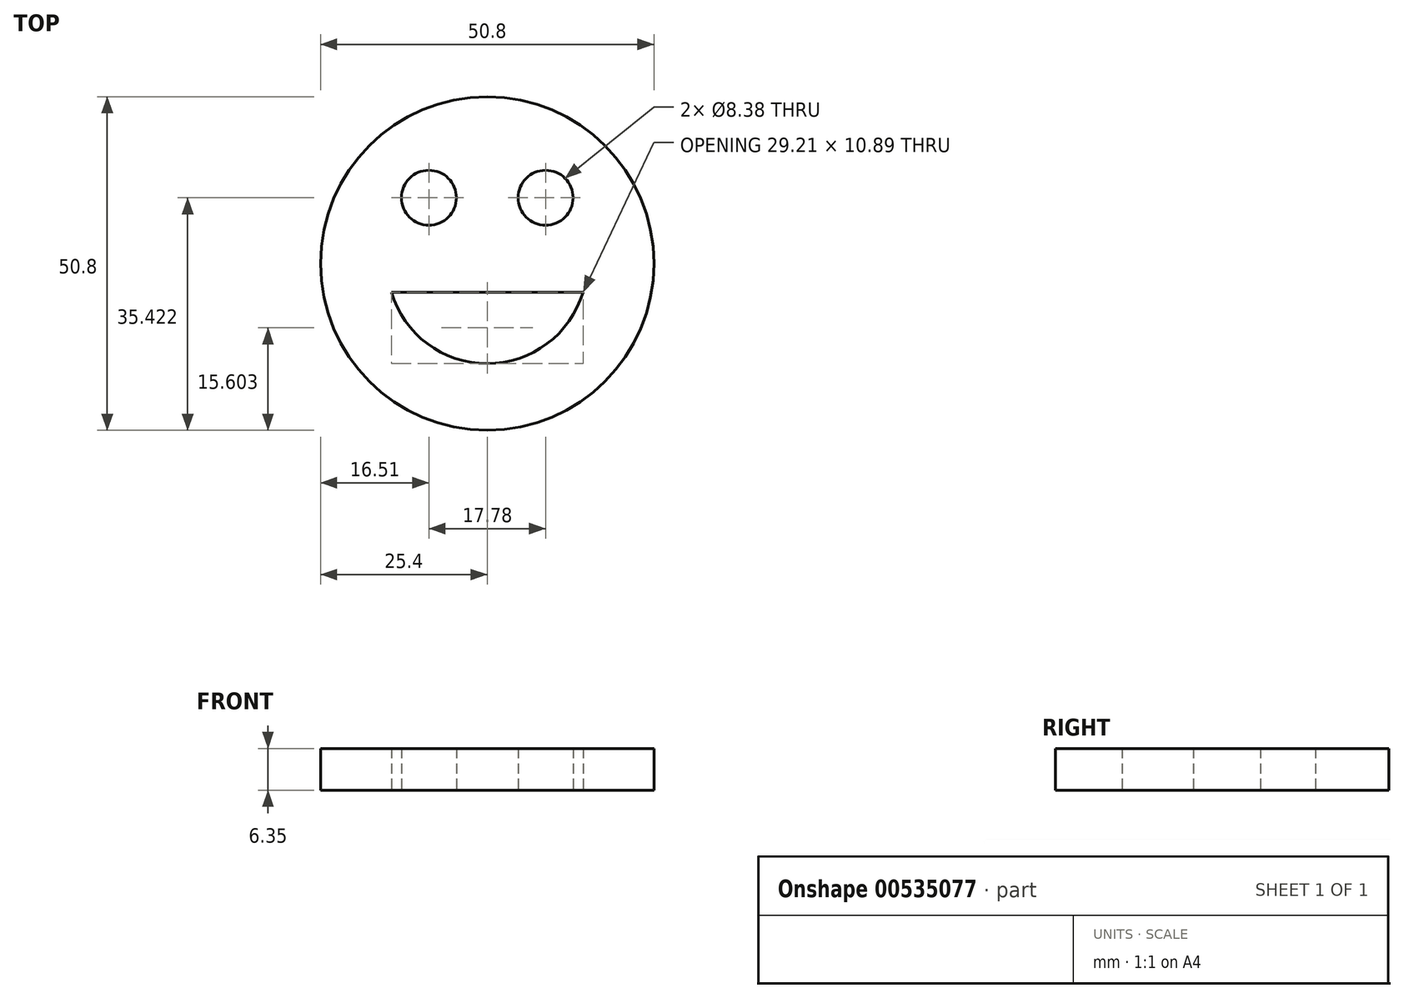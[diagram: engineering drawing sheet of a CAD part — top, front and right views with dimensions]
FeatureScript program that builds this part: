
annotation { "Feature Type Name" : "Feature", "Feature Type Description" : "" }
export const myFeature = defineFeature(function(context is Context, id is Id, definition is map)
    precondition{}
    {
        {
            var Q0;
            Q0=qCreatedBy(makeId("Top.planeOp"),FACE);
            var sketch = newSketch(context, id + "F0", { "sketchPlane" : qUnion([Q0])});
            skCircle(sketch, "E0", {"center": v(0, 0) * mm, "radius": 25.4 * mm});
            skCircle(sketch, "E1", {"center": v(-8.9, 10.02) * mm, "radius": 4.2 * mm});
            skCircle(sketch, "E2", {"center": v(8.9, 10.02) * mm, "radius": 4.2 * mm});
            skArc(sketch, "E3", {"start": v(-14.6, -4.35) * mm, "mid": v(0, -15.24) * mm, "end": v(14.6, -4.35) * mm});
            skLineSegment(sketch, "E4", {"start": v(-14.6, -4.35) * mm, "end": v(14.6, -4.35) * mm});
            skSolve(sketch);
        }
        {
            var Q0;
            Q0 = qSketchRegion(id + "F0", true);
            extrude(context, id + "F1", {"entities" : qUnion([Q0]), "depth" : 6.35 * mm, "offsetDistance" : 25.4 * mm});
        }
    });
